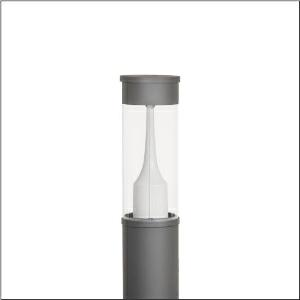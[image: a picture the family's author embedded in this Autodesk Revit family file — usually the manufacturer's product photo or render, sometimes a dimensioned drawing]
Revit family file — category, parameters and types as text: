
# Revit family: city-light_120_iq___p1_0a_5xa5285lf14h_baf3
name_source: partatom
category: Lighting Fixtures
units: mm (PartAtom-declared; Revit-internal decimal feet)

## family parameters
Cut with Voids When Loaded = No
Host = Face
Light Source = No
Part Type = Normal
Room Calculation Point = No
Round Connector Dimension = Use Diameter
Shared = No

## types (1)
- --- (1 x LED, 1510 lm, 10 W, 4000K)
    Apparent Load = 10 VA
    CIE Flux Codes = 32 61 90 93 100
    Color Rendering = 70
    Color Temperature = 4000K
    Default Elevation = 1800 mm
    Description = City-Light 120 iQ, bollard luminaire, Module 540 iQ-SR, primary light control with 3 zone facetted reflector, of plastic, silver coated, highly specular, structured, primary optical cover: cover, of PMMA, transparent, partly coated, light distribution: P1.0a, primary light characteristic: strongly asymmetric, LED, High Power LED, rated luminous flux: 1.510lm, luminous efficacy: 151lm/W, light colour: 740, colour temperature: 4000K, control gear: ECG iQ, control: presetting dimming logarithmic, Street-Remote, Auto-Match, Temp-Guard, Lumen-Switch, Night-Set, Smart-Wire, Light-Fading, Desk-Remote (wireless, voltage-free reading and setting of iQ features in the workshop via application-optimized NFC function/RFID function), optimised constant luminous flux control (CLO 2.0), with terminal, 6-pole, max. 2.5mm², mains connection: 230..240V, AC, 50/60Hz, start of lifetime: 10W, end of service life: 10W, reduction: 5W, luminaire housing, cylindrical, of extruded aluminium section, coated, Siteco® metallic grey (DB 702S), length: 1.200mm, diameter: 200mm, Module 540 iQ-SR, traffic white (RAL 9016), equipment: standard, protection rating (complete): IP54, insulation class (complete): insulation class II (safety insulation), certification: CE, ENEC, VDE, packaging unit: 1 piece

Light Distribution: P1.0a
    Height = 500 mm
    Lamp = 1 x LED
    Lamp Light Flux = 1510 lm
    Lamp Power = 10 W
    Lamp count = 1
    Length = 200 mm  [stored 0.656168 ft]
    Luminous efficacy = 151 lm/W
    Manufacturer = Siteco
    ModVariant = No
    Model = 5XA5285LF14H
    Mounting Place = Floor
    Mounting Type = Freestanding
    Number of Poles = 1
    OnlyDefault = Yes
    Power Factor = 1
    Product Name = City-Light 120 iQ | P1.0a
    Product group = bollard luminaire
    ProductGroupID = 1304
    Protection Class = Protection class II
    Protection Degree = IP 54
    RLX_Detail_Level = 1
    RLX_Emergency_Light_Flux = 0 lm
    RLX_Emergency_Type = 0
    RLX_Emergency_Type_DB = No
    RlxData = <blob elided: 52533 chars, md5=098c3e75>
    Socket = socket
    Standby Power = 0 W
    System Light Flux = 1510 lm
    System Power = 10 W
    Type Comments = factory setting: luminous flux: 100 % | dim-lin: 254 | 401 mA
    Type Image = l_1006922.jpg
    URL = http://relux.com
    VarID = @adj_091887
    Voltage = 0 V
    Weight = 0.00 kg
    Width = 0 mm  [stored 0 ft]

note: [stored X ft] marks values corroborated as IEEE doubles in the binary element streams (Revit-internal decimal feet)

## geometry (parser evidence)
native form markers: Blend x4, Sweep x13
no freeform markers — native parametric forms only
